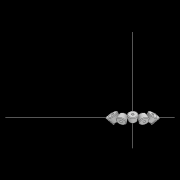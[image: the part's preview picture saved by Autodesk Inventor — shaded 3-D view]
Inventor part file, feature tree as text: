
AUTODESK INVENTOR PART (.ipt)
format: ipt  version: 2022.2 (Build 262287010, 287A)  size: 765,952 bytes
history: native  units: mm
features: extrude x19, sketch x18, pattern_circular x15, other x14, revolve x7, hole x7, move_body x4, fillet x2, draft x2
ambient origin geometry x8: Origin, YZ Plane, XZ Plane, XY Plane, X Axis, Y Axis, Z Axis, Center Point
bodies: Solid1 (feature_tree), Solid2 (feature_tree), Solid3 (feature_tree), Solid4 (feature_tree), Solid5 (feature_tree)
feature tree (88):
  sketch  "Sketch7"  dims[d21=0.5mm]
  other  "Roller1"
  other  "Roller2"
  sketch  "Sketch22"  dims[d39=0.05mm]
  sketch  "Sketch2"  dims[d17=0.05mm]
  sketch  "Sketch23"  dims[d41=0.05mm]
  other  "RevRoller1"
  fillet  "Fillet1"  Radius=0.05mm
  pattern_circular  "Circular Pattern13"  Count=6  [1 undecoded]
  move_body  "Move Body7"
  revolve  "Revolution13"  Angle=30.0deg
  fillet  "Fillet3"  [1 undecoded]
  pattern_circular  "Circular Pattern14"  [2 undecoded]
  move_body  "Move Body6"
  revolve  "Revolution14"  [1 undecoded]
  other  "OuterRim_Top2"
  other  "OuterRim_Bottom2"
  extrude  "Extrusion9"  TaperAngle=90.0deg  [1 undecoded]
  sketch  "Sketch24"  dims[d42=0.5mm]
  extrude  "Extrusion10"  Depth=0.5mm
  extrude  "Extrusion11"  Depth=0.5mm
  pattern_circular  "Circular Pattern15"  [2 undecoded]
  sketch  "Sketch25"  dims[d43=0.5mm]
  extrude  "Extrusion12"  Depth=0.5mm
  extrude  "Extrusion14"  Depth=0.5mm
  extrude  "Extrusion15"  Depth=0.5mm
  pattern_circular  "Circular Pattern16"  [2 undecoded]
  extrude  "Extrusion16"  Depth=0.5mm
  extrude  "Extrusion17"  Depth=0.5mm
  hole  "Hole9"  [1 undecoded]
  pattern_circular  "Circular Pattern17"  [2 undecoded]
  sketch  "Sketch27"  dims[d45=0.5mm]
  hole  "Hole10"  [1 undecoded]
  hole  "Hole11"  [1 undecoded]
  pattern_circular  "Circular Pattern18"  [2 undecoded]
  extrude  "Extrusion18"  Depth=0.5mm
  extrude  "Extrusion19"  Depth=0.5mm
  pattern_circular  "Circular Pattern19"  [2 undecoded]
  sketch  "Sketch28"  dims[d46=0.5mm d47=0.5mm d48=2.0mm d50=90.0deg d56=14.029612mm d57=4.025mm d90=16.473921mm d107=0.05mm d108=0.05mm d109=0.05mm d110=0.05mm d112=0.5mm d113=0.5mm d114=0.5mm d115=14.644822mm d116=14.607374mm d117=1.0mm d118=0.05mm d119=0.05mm d120=0.05mm d121=0.05mm d122=0.5mm d123=0.5mm d124=14.644822mm d125=14.607374mm d126=1.0mm d127=90.0deg d128=30.0deg d129=90.0deg d167=8.972256mm d173=10.814812mm d201=55.5mm d202=90.0deg d203=90.0deg d204=90.0deg d218=55.5mm d226=5.4mm d232=0.0mm d233=3600.0mm d234=10.502mm d235=0.0mm d243=1.902mm d244=0.0mm d246=2.75mm d247=5.251mm d248=0.0mm d249=3.0mm d250=0.0mm d251=90.0mm d252=360.0deg d254=2.75mm d255=3.0mm d256=5.251mm d257=0.0mm d258=3.0mm d259=0.0mm d260=90.0mm d261=360.0deg d277=76.5mm d281=73.5mm d282=24.65mm d283=6.0mm d284=4.0mm d285=2.0mm d286=90.0deg d287=5.251mm d288=0.0mm d289=60.0mm d290=360.0deg d292=0.436332mm d293=60.0mm d294=90.0mm d295=3.0mm d296=6.0mm d297=5.5mm d298=3.0mm d299=90.0deg d300=5.251mm d301=0.0mm d302=60.0mm d303=360.0deg d305=30.0deg d306=73.5mm d307=24.65mm d308=6.0mm d309=5.5mm d310=3.0mm d311=90.0deg d312=5.251mm d313=0.0mm d314=60.0mm d315=360.0deg d317=90.0mm d318=60.0mm d319=30.0deg d320=5.4mm d321=5.4mm d322=3.0mm d323=6.0mm d324=5.5mm d325=3.0mm d326=90.0deg d327=5.251mm d328=0.0mm d329=2.4mm d330=0.0mm d331=60.0mm d332=360.0deg d343=17.307186mm d344=17.309884mm d345=0.025mm d346=0.025mm d347=0.1mm d348=0.1mm d349=17.309884mm d350=17.307186mm d351=0.025mm d352=0.025mm d354=0.1mm d355=17.307186mm d356=17.309884mm d357=1.0mm d358=90.0deg d359=0.5mm d360=60.0mm d361=360.0deg d363=30.0deg d367=8.1mm d369=4.014775mm d370=0.1mm d371=1.0mm d372=30.0deg d373=90.0deg d374=0.5mm d375=60.0mm d376=360.0deg d378=90.0deg d379=0.1mm d380=0.1mm d381=0.1mm d382=0.1mm d383=0.1mm d384=10.502mm d385=0.0mm d386=0.0mm d391=1.0mm d392=55.5mm d393=1.5mm d394=1.5mm d395=1.5mm d396=1.5mm d397=90.0deg d398=90.0deg d399=90.0deg d400=55.5mm d401=10.502mm d402=0.0mm d403=2.75mm d404=1.5mm d405=10.502mm d406=0.0mm d407=3.0mm d408=0.0mm d409=90.0mm d410=360.0deg d412=5.4mm d413=5.251mm d414=0.0mm d417=5.4mm d418=2.4mm d419=0.0mm d420=2.4mm d421=0.0mm d422=90.0mm d423=360.0deg d425=60.0mm d426=90.0mm d427=1.5mm d428=1.5mm d429=5.4mm d430=5.4mm d431=5.251mm d432=0.0mm d433=2.4mm d434=0.0mm d435=30.0deg d436=73.5mm d437=24.65mm d438=6.0mm d439=4.0mm d440=2.0mm d441=90.0deg d442=5.251mm d443=0.0mm d444=60.0mm d445=360.0deg d447=3.0mm d448=6.0mm d449=5.5mm d450=3.0mm d451=90.0deg d452=5.251mm d453=0.0mm d454=24.65mm d455=6.0mm d456=5.5mm d457=3.0mm d458=90.0deg d459=5.251mm d460=0.0mm d461=60.0mm d462=360.0deg d464=5.251mm d465=0.0mm d466=3.0mm d467=0.0mm d468=90.0mm d469=360.0deg d472=1.5mm d474=5.251mm d475=0.0mm d481=3.0mm d482=0.0mm d483=90.0mm d484=360.0deg d486=0.436332mm d49=0.872665mm d51=0.872665mm d52=0.872665mm d236=0.5mm d237=0.872665mm d238=0.5mm d239=0.872665mm d291=0.0625mm d415=0.5mm d416=0.872665mm d471=0.5mm d473=0.5mm]
  extrude  "Extrusion20"  Depth=0.5mm
  extrude  "Extrusion22"  Depth=0.5mm
  pattern_circular  "Circular Pattern21"  [2 undecoded]
  draft  "FaceDraft2"
  other  "InnerRim"
  other  "OuterRim_Top"
  other  "OuterRim_Bottom"
  extrude  "Extrusion2"  Depth=0.5mm
  sketch  "Sketch13"  dims[d24=0.5mm]
  extrude  "Extrusion3"  Depth=1.0mm
  sketch  "Sketch15"  dims[d29=360.0deg d30=60.0mm]
  extrude  "Extrusion4"  TaperAngle=90.0deg  [1 undecoded]
  extrude  "Extrusion5"  TaperAngle=30.0deg  [1 undecoded]
  pattern_circular  "Circular Pattern6"  Angle=90.0deg  [1 undecoded]
  sketch  "Sketch16"  dims[d31=360.0deg d35=30.0deg d36=90.0deg]
  extrude  "Extrusion6"  Depth=0.5mm
  extrude  "Extrusion7"  Depth=0.5mm
  pattern_circular  "Circular Pattern7"  [2 undecoded]
  hole  "Hole5"  [1 undecoded]
  pattern_circular  "Circular Pattern9"  Angle=90.0deg  [1 undecoded]
  draft  "FaceDraft1"
  hole  "Hole6"  [1 undecoded]
  pattern_circular  "Circular Pattern10"  [2 undecoded]
  hole  "Hole7"  [1 undecoded]
  pattern_circular  "Circular Pattern11"  Count=360  [1 undecoded]
  hole  "Hole8"  [1 undecoded]
  extrude  "Extrusion8"  TaperAngle=0.0deg  [1 undecoded]
  pattern_circular  "Circular Pattern12"  [2 undecoded]
  sketch  "Sketch8"  dims[d22=0.5mm]
  sketch  "Sketch9"  dims[d23=0.5mm]
  revolve  "Revolution4"  [1 undecoded]
  move_body  "Move Body4"
  revolve  "Revolution5"  [1 undecoded]
  sketch  "Sketch5"  dims[d19=0.5mm]
  sketch  "Sketch6"  dims[d20=0.5mm]
  revolve  "Revolution3"  [1 undecoded]
  sketch  "Sketch4"  dims[d18=0.05mm]
  revolve  "Revolution1"  [1 undecoded]
  pattern_circular  "Circular Pattern1"  [2 undecoded]
  move_body  "Move Body3"
  revolve  "Revolution2"  [1 undecoded]
  other  "2D Equation Curve1"
  sketch  "Sketch14"  dims[d28=2.0mm]
  other  "Work Axis1"
  other  "Work Axis2"
  other  "Work Axis3"
  other  "Work Axis4"
  other  "Work Axis5"
  sketch  "Sketch26"  dims[d44=0.5mm]
note: 44 required parameter values undecoded (feature->parameter linkage not recoverable at this tier; creation-order binding heuristic only, values carry confidence <= 0.55)